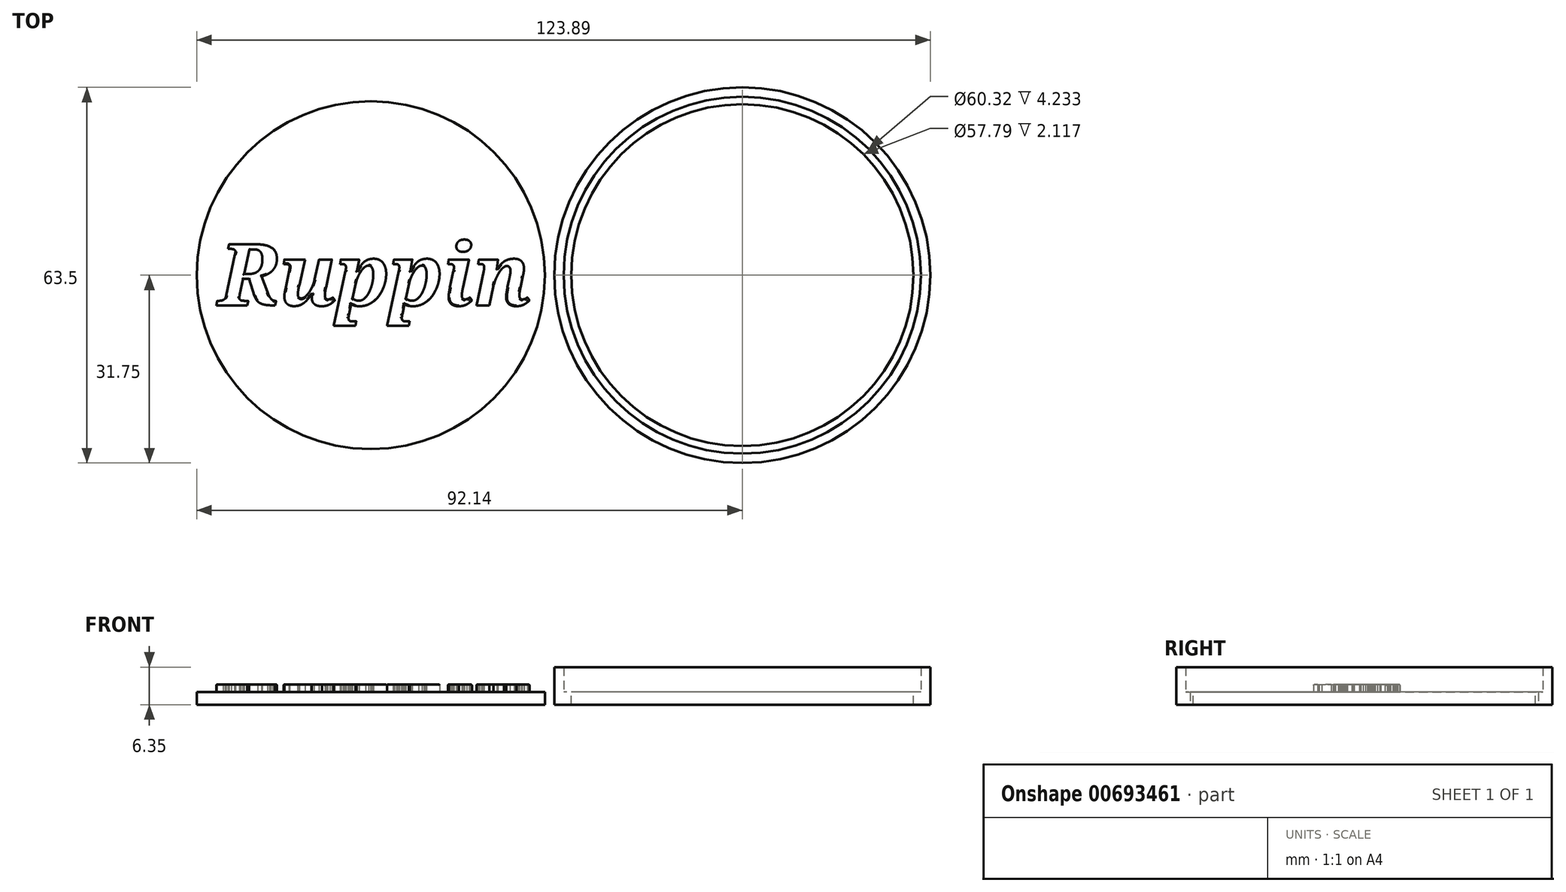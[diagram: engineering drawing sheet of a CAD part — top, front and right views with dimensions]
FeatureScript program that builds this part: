
annotation { "Feature Type Name" : "Feature", "Feature Type Description" : "" }
export const myFeature = defineFeature(function(context is Context, id is Id, definition is map)
    precondition{}
    {
        {
            var Q0;
            Q0=qCreatedBy(makeId("Top.planeOp"),FACE);
            var sketch = newSketch(context, id + "F0", { "sketchPlane" : qUnion([Q0])});
            skCircle(sketch, "E0", {"center": v(0, 0) * mm, "radius": 31.75 * mm});
            skCircle(sketch, "E1.0", {"center": v(0, 0) * mm, "radius": 30.16 * mm});
            skCircle(sketch, "E2.0", {"center": v(0, 0) * mm, "radius": 28.9 * mm});
            skCircle(sketch, "E3.0", {"center": v(0, 0) * mm, "radius": 29.4 * mm});
            skSolve(sketch);
        }
        {
            var Q0;
            Q0=makeQuery(id+"F0.imprint","IMPRINT",FACE,{"disambiguationData":[TD([[makeQuery(id+"F0.imprint","IMPRINT",EDGE,{"derivedFrom":sQuery(id+"F0.wireOp",EDGE,"E0")}),1.0]])]});
            extrude(context, id + "F1", {"entities" : qUnion([Q0]), "depth" : 2.12 * mm, "offsetDistance" : 25.4 * mm});
        }
        {
            var Q0;
            Q0=makeQuery(id+"F1.opExtrude","CAP_FACE",FACE,{"disambiguationData":[OSD([sQuery(id+"F0.wireOp",EDGE,"E0"),sQuery(id+"F0.wireOp",EDGE,"E1.0")])],"isStart":false});
            extrude(context, id + "F2", {"entities" : qUnion([Q0]), "operationType" : NewBodyOperationType.ADD, "depth" : 2.12 * mm, "offsetDistance" : 25.4 * mm});
        }
        {
            var Q0;
            Q0=makeQuery(id+"F0.imprint","IMPRINT",FACE,{"disambiguationData":[TD([[makeQuery(id+"F0.imprint","IMPRINT",EDGE,{"derivedFrom":sQuery(id+"F0.wireOp",EDGE,"E1.0")}),1.0]])]});
            var Q1;
            Q1=makeQuery(id+"F0.imprint","IMPRINT",FACE,{"disambiguationData":[TD([[makeQuery(id+"F0.imprint","IMPRINT",EDGE,{"derivedFrom":sQuery(id+"F0.wireOp",EDGE,"E0")}),1.0]])]});
            var Q2;
            Q2=makeQuery(id+"F0.imprint","IMPRINT",FACE,{"disambiguationData":[TD([[makeQuery(id+"F0.imprint","IMPRINT",EDGE,{"derivedFrom":sQuery(id+"F0.wireOp",EDGE,"E2.0")}),-1.0]])]});
            extrude(context, id + "F3", {"entities" : qUnion([Q0, Q1, Q2]), "operationType" : NewBodyOperationType.ADD, "oppositeDirection" : true, "depth" : 2.12 * mm, "offsetDistance" : 25.4 * mm});
        }
        {
            var Q0;
            Q0=makeQuery(id+"F0.imprint","IMPRINT",FACE,{"disambiguationData":[TD([[makeQuery(id+"F0.imprint","IMPRINT",EDGE,{"derivedFrom":sQuery(id+"F0.wireOp",EDGE,"E2.0")}),1.0]])]});
            var Q1;
            Q1=makeQuery(id+"F0.imprint","IMPRINT",FACE,{"disambiguationData":[TD([[makeQuery(id+"F0.imprint","IMPRINT",EDGE,{"derivedFrom":sQuery(id+"F0.wireOp",EDGE,"E2.0")}),-1.0]])]});
            extrude(context, id + "F4", {"entities" : qUnion([Q0, Q1]), "depth" : 2.12 * mm, "offsetDistance" : 25.4 * mm});
        }
        {
            var Q0;
            Q0=makeQuery(id+"F4.opExtrude","CAP_FACE",FACE,{"disambiguationData":[OSD([sQuery(id+"F0.wireOp",EDGE,"E3.0")])],"isStart":false});
            var sketch = newSketch(context, id + "F5", { "sketchPlane" : qUnion([Q0])});
            skText(sketch, "E4", { "text": "Ruppin", "fontName": "NotoSerif-BoldItalic.ttf"});
            const initialGuessF5  = {"E4": [-0.02578, -0.00511, 1, 0, 0.01041]};
            skSetInitialGuess(sketch, initialGuessF5);
            skSolve(sketch);
        }
        {
            var Q0;
            Q0=qSketchRegion(id+"F5",true);
            extrude(context, id + "F6", {"entities" : qUnion([Q0]), "operationType" : NewBodyOperationType.ADD, "depth" : 1.27 * mm, "offsetDistance" : 25.4 * mm});
        }
        {
            var Q0;
            Q0=makeQuery(id+"F6.opExtrude","CAP_FACE",FACE,{"disambiguationData":[OSD([sQuery(id+"F5.wireOp",EDGE,"E4.sketch_text.stroke-0"),sQuery(id+"F5.wireOp",EDGE,"E4.sketch_text.stroke-1"),sQuery(id+"F5.wireOp",EDGE,"E4.sketch_text.stroke-2"),sQuery(id+"F5.wireOp",EDGE,"E4.sketch_text.stroke-3"),sQuery(id+"F5.wireOp",EDGE,"E4.sketch_text.stroke-4"),sQuery(id+"F5.wireOp",EDGE,"E4.sketch_text.stroke-5"),sQuery(id+"F5.wireOp",EDGE,"E4.sketch_text.stroke-6"),sQuery(id+"F5.wireOp",EDGE,"E4.sketch_text.stroke-7"),sQuery(id+"F5.wireOp",EDGE,"E4.sketch_text.stroke-8"),sQuery(id+"F5.wireOp",EDGE,"E4.sketch_text.stroke-9"),sQuery(id+"F5.wireOp",EDGE,"E4.sketch_text.stroke-10"),sQuery(id+"F5.wireOp",EDGE,"E4.sketch_text.stroke-11"),sQuery(id+"F5.wireOp",EDGE,"E4.sketch_text.stroke-12"),sQuery(id+"F5.wireOp",EDGE,"E4.sketch_text.stroke-13"),sQuery(id+"F5.wireOp",EDGE,"E4.sketch_text.stroke-14"),sQuery(id+"F5.wireOp",EDGE,"E4.sketch_text.stroke-15"),sQuery(id+"F5.wireOp",EDGE,"E4.sketch_text.stroke-16"),sQuery(id+"F5.wireOp",EDGE,"E4.sketch_text.stroke-17"),sQuery(id+"F5.wireOp",EDGE,"E4.sketch_text.stroke-18"),sQuery(id+"F5.wireOp",EDGE,"E4.sketch_text.stroke-19"),sQuery(id+"F5.wireOp",EDGE,"E4.sketch_text.stroke-20"),sQuery(id+"F5.wireOp",EDGE,"E4.sketch_text.stroke-21"),sQuery(id+"F5.wireOp",EDGE,"E4.sketch_text.stroke-22"),sQuery(id+"F5.wireOp",EDGE,"E4.sketch_text.stroke-23"),sQuery(id+"F5.wireOp",EDGE,"E4.sketch_text.stroke-24"),sQuery(id+"F5.wireOp",EDGE,"E4.sketch_text.stroke-25"),sQuery(id+"F5.wireOp",EDGE,"E4.sketch_text.stroke-26"),sQuery(id+"F5.wireOp",EDGE,"E4.sketch_text.stroke-27"),sQuery(id+"F5.wireOp",EDGE,"E4.sketch_text.stroke-28"),sQuery(id+"F5.wireOp",EDGE,"E4.sketch_text.stroke-29"),sQuery(id+"F5.wireOp",EDGE,"E4.sketch_text.stroke-30"),sQuery(id+"F5.wireOp",EDGE,"E4.sketch_text.stroke-31"),sQuery(id+"F5.wireOp",EDGE,"E4.sketch_text.stroke-32"),sQuery(id+"F5.wireOp",EDGE,"E4.sketch_text.stroke-33"),sQuery(id+"F5.wireOp",EDGE,"E4.sketch_text.stroke-34"),sQuery(id+"F5.wireOp",EDGE,"E4.sketch_text.stroke-35"),sQuery(id+"F5.wireOp",EDGE,"E4.sketch_text.stroke-36"),sQuery(id+"F5.wireOp",EDGE,"E4.sketch_text.stroke-37"),sQuery(id+"F5.wireOp",EDGE,"E4.sketch_text.stroke-38"),sQuery(id+"F5.wireOp",EDGE,"E4.sketch_text.stroke-39"),sQuery(id+"F5.wireOp",EDGE,"E4.sketch_text.stroke-40"),sQuery(id+"F5.wireOp",EDGE,"E4.sketch_text.stroke-41"),sQuery(id+"F5.wireOp",EDGE,"E4.sketch_text.stroke-42"),sQuery(id+"F5.wireOp",EDGE,"E4.sketch_text.stroke-43"),sQuery(id+"F5.wireOp",EDGE,"E4.sketch_text.stroke-44"),sQuery(id+"F5.wireOp",EDGE,"E4.sketch_text.stroke-45"),sQuery(id+"F5.wireOp",EDGE,"E4.sketch_text.stroke-46"),sQuery(id+"F5.wireOp",EDGE,"E4.sketch_text.stroke-47"),sQuery(id+"F5.wireOp",EDGE,"E4.sketch_text.stroke-48"),sQuery(id+"F5.wireOp",EDGE,"E4.sketch_text.stroke-49"),sQuery(id+"F5.wireOp",EDGE,"E4.sketch_text.stroke-50"),sQuery(id+"F5.wireOp",EDGE,"E4.sketch_text.stroke-51"),sQuery(id+"F5.wireOp",EDGE,"E4.sketch_text.stroke-52"),sQuery(id+"F5.wireOp",EDGE,"E4.sketch_text.stroke-53"),sQuery(id+"F5.wireOp",EDGE,"E4.sketch_text.stroke-54"),sQuery(id+"F5.wireOp",EDGE,"E4.sketch_text.stroke-55")])],"isStart":false});
            var Q1;
            Q1=makeQuery(id+"F6.opExtrude","CAP_FACE",FACE,{"disambiguationData":[OSD([sQuery(id+"F5.wireOp",EDGE,"E4.sketch_text.stroke-56"),sQuery(id+"F5.wireOp",EDGE,"E4.sketch_text.stroke-57"),sQuery(id+"F5.wireOp",EDGE,"E4.sketch_text.stroke-58"),sQuery(id+"F5.wireOp",EDGE,"E4.sketch_text.stroke-59"),sQuery(id+"F5.wireOp",EDGE,"E4.sketch_text.stroke-60"),sQuery(id+"F5.wireOp",EDGE,"E4.sketch_text.stroke-61"),sQuery(id+"F5.wireOp",EDGE,"E4.sketch_text.stroke-62"),sQuery(id+"F5.wireOp",EDGE,"E4.sketch_text.stroke-63"),sQuery(id+"F5.wireOp",EDGE,"E4.sketch_text.stroke-64"),sQuery(id+"F5.wireOp",EDGE,"E4.sketch_text.stroke-65"),sQuery(id+"F5.wireOp",EDGE,"E4.sketch_text.stroke-66"),sQuery(id+"F5.wireOp",EDGE,"E4.sketch_text.stroke-67"),sQuery(id+"F5.wireOp",EDGE,"E4.sketch_text.stroke-68"),sQuery(id+"F5.wireOp",EDGE,"E4.sketch_text.stroke-69"),sQuery(id+"F5.wireOp",EDGE,"E4.sketch_text.stroke-70"),sQuery(id+"F5.wireOp",EDGE,"E4.sketch_text.stroke-71"),sQuery(id+"F5.wireOp",EDGE,"E4.sketch_text.stroke-72"),sQuery(id+"F5.wireOp",EDGE,"E4.sketch_text.stroke-73"),sQuery(id+"F5.wireOp",EDGE,"E4.sketch_text.stroke-74"),sQuery(id+"F5.wireOp",EDGE,"E4.sketch_text.stroke-75"),sQuery(id+"F5.wireOp",EDGE,"E4.sketch_text.stroke-76"),sQuery(id+"F5.wireOp",EDGE,"E4.sketch_text.stroke-77"),sQuery(id+"F5.wireOp",EDGE,"E4.sketch_text.stroke-78"),sQuery(id+"F5.wireOp",EDGE,"E4.sketch_text.stroke-79"),sQuery(id+"F5.wireOp",EDGE,"E4.sketch_text.stroke-80"),sQuery(id+"F5.wireOp",EDGE,"E4.sketch_text.stroke-81"),sQuery(id+"F5.wireOp",EDGE,"E4.sketch_text.stroke-82"),sQuery(id+"F5.wireOp",EDGE,"E4.sketch_text.stroke-83"),sQuery(id+"F5.wireOp",EDGE,"E4.sketch_text.stroke-84"),sQuery(id+"F5.wireOp",EDGE,"E4.sketch_text.stroke-85"),sQuery(id+"F5.wireOp",EDGE,"E4.sketch_text.stroke-86"),sQuery(id+"F5.wireOp",EDGE,"E4.sketch_text.stroke-87"),sQuery(id+"F5.wireOp",EDGE,"E4.sketch_text.stroke-88"),sQuery(id+"F5.wireOp",EDGE,"E4.sketch_text.stroke-89"),sQuery(id+"F5.wireOp",EDGE,"E4.sketch_text.stroke-90"),sQuery(id+"F5.wireOp",EDGE,"E4.sketch_text.stroke-91"),sQuery(id+"F5.wireOp",EDGE,"E4.sketch_text.stroke-92"),sQuery(id+"F5.wireOp",EDGE,"E4.sketch_text.stroke-93"),sQuery(id+"F5.wireOp",EDGE,"E4.sketch_text.stroke-94"),sQuery(id+"F5.wireOp",EDGE,"E4.sketch_text.stroke-95"),sQuery(id+"F5.wireOp",EDGE,"E4.sketch_text.stroke-96"),sQuery(id+"F5.wireOp",EDGE,"E4.sketch_text.stroke-97"),sQuery(id+"F5.wireOp",EDGE,"E4.sketch_text.stroke-98"),sQuery(id+"F5.wireOp",EDGE,"E4.sketch_text.stroke-99"),sQuery(id+"F5.wireOp",EDGE,"E4.sketch_text.stroke-100"),sQuery(id+"F5.wireOp",EDGE,"E4.sketch_text.stroke-101"),sQuery(id+"F5.wireOp",EDGE,"E4.sketch_text.stroke-102"),sQuery(id+"F5.wireOp",EDGE,"E4.sketch_text.stroke-103"),sQuery(id+"F5.wireOp",EDGE,"E4.sketch_text.stroke-104"),sQuery(id+"F5.wireOp",EDGE,"E4.sketch_text.stroke-105"),sQuery(id+"F5.wireOp",EDGE,"E4.sketch_text.stroke-106"),sQuery(id+"F5.wireOp",EDGE,"E4.sketch_text.stroke-107")])],"isStart":false});
            var Q2;
            Q2=makeQuery(id+"F6.opExtrude","CAP_FACE",FACE,{"disambiguationData":[OSD([sQuery(id+"F5.wireOp",EDGE,"E4.sketch_text.stroke-108"),sQuery(id+"F5.wireOp",EDGE,"E4.sketch_text.stroke-109"),sQuery(id+"F5.wireOp",EDGE,"E4.sketch_text.stroke-110"),sQuery(id+"F5.wireOp",EDGE,"E4.sketch_text.stroke-111"),sQuery(id+"F5.wireOp",EDGE,"E4.sketch_text.stroke-112"),sQuery(id+"F5.wireOp",EDGE,"E4.sketch_text.stroke-113"),sQuery(id+"F5.wireOp",EDGE,"E4.sketch_text.stroke-114"),sQuery(id+"F5.wireOp",EDGE,"E4.sketch_text.stroke-115"),sQuery(id+"F5.wireOp",EDGE,"E4.sketch_text.stroke-116"),sQuery(id+"F5.wireOp",EDGE,"E4.sketch_text.stroke-117"),sQuery(id+"F5.wireOp",EDGE,"E4.sketch_text.stroke-118"),sQuery(id+"F5.wireOp",EDGE,"E4.sketch_text.stroke-119"),sQuery(id+"F5.wireOp",EDGE,"E4.sketch_text.stroke-120"),sQuery(id+"F5.wireOp",EDGE,"E4.sketch_text.stroke-121"),sQuery(id+"F5.wireOp",EDGE,"E4.sketch_text.stroke-122"),sQuery(id+"F5.wireOp",EDGE,"E4.sketch_text.stroke-123"),sQuery(id+"F5.wireOp",EDGE,"E4.sketch_text.stroke-124"),sQuery(id+"F5.wireOp",EDGE,"E4.sketch_text.stroke-125"),sQuery(id+"F5.wireOp",EDGE,"E4.sketch_text.stroke-126"),sQuery(id+"F5.wireOp",EDGE,"E4.sketch_text.stroke-127"),sQuery(id+"F5.wireOp",EDGE,"E4.sketch_text.stroke-128"),sQuery(id+"F5.wireOp",EDGE,"E4.sketch_text.stroke-129"),sQuery(id+"F5.wireOp",EDGE,"E4.sketch_text.stroke-130"),sQuery(id+"F5.wireOp",EDGE,"E4.sketch_text.stroke-131"),sQuery(id+"F5.wireOp",EDGE,"E4.sketch_text.stroke-132"),sQuery(id+"F5.wireOp",EDGE,"E4.sketch_text.stroke-133"),sQuery(id+"F5.wireOp",EDGE,"E4.sketch_text.stroke-134"),sQuery(id+"F5.wireOp",EDGE,"E4.sketch_text.stroke-135"),sQuery(id+"F5.wireOp",EDGE,"E4.sketch_text.stroke-136"),sQuery(id+"F5.wireOp",EDGE,"E4.sketch_text.stroke-137"),sQuery(id+"F5.wireOp",EDGE,"E4.sketch_text.stroke-138"),sQuery(id+"F5.wireOp",EDGE,"E4.sketch_text.stroke-139"),sQuery(id+"F5.wireOp",EDGE,"E4.sketch_text.stroke-140"),sQuery(id+"F5.wireOp",EDGE,"E4.sketch_text.stroke-141"),sQuery(id+"F5.wireOp",EDGE,"E4.sketch_text.stroke-142"),sQuery(id+"F5.wireOp",EDGE,"E4.sketch_text.stroke-143"),sQuery(id+"F5.wireOp",EDGE,"E4.sketch_text.stroke-144"),sQuery(id+"F5.wireOp",EDGE,"E4.sketch_text.stroke-145"),sQuery(id+"F5.wireOp",EDGE,"E4.sketch_text.stroke-146"),sQuery(id+"F5.wireOp",EDGE,"E4.sketch_text.stroke-147"),sQuery(id+"F5.wireOp",EDGE,"E4.sketch_text.stroke-148"),sQuery(id+"F5.wireOp",EDGE,"E4.sketch_text.stroke-149"),sQuery(id+"F5.wireOp",EDGE,"E4.sketch_text.stroke-150"),sQuery(id+"F5.wireOp",EDGE,"E4.sketch_text.stroke-151"),sQuery(id+"F5.wireOp",EDGE,"E4.sketch_text.stroke-152"),sQuery(id+"F5.wireOp",EDGE,"E4.sketch_text.stroke-153"),sQuery(id+"F5.wireOp",EDGE,"E4.sketch_text.stroke-154"),sQuery(id+"F5.wireOp",EDGE,"E4.sketch_text.stroke-155"),sQuery(id+"F5.wireOp",EDGE,"E4.sketch_text.stroke-156"),sQuery(id+"F5.wireOp",EDGE,"E4.sketch_text.stroke-157"),sQuery(id+"F5.wireOp",EDGE,"E4.sketch_text.stroke-158"),sQuery(id+"F5.wireOp",EDGE,"E4.sketch_text.stroke-159"),sQuery(id+"F5.wireOp",EDGE,"E4.sketch_text.stroke-160"),sQuery(id+"F5.wireOp",EDGE,"E4.sketch_text.stroke-161"),sQuery(id+"F5.wireOp",EDGE,"E4.sketch_text.stroke-162"),sQuery(id+"F5.wireOp",EDGE,"E4.sketch_text.stroke-163"),sQuery(id+"F5.wireOp",EDGE,"E4.sketch_text.stroke-164"),sQuery(id+"F5.wireOp",EDGE,"E4.sketch_text.stroke-165"),sQuery(id+"F5.wireOp",EDGE,"E4.sketch_text.stroke-166"),sQuery(id+"F5.wireOp",EDGE,"E4.sketch_text.stroke-167"),sQuery(id+"F5.wireOp",EDGE,"E4.sketch_text.stroke-168"),sQuery(id+"F5.wireOp",EDGE,"E4.sketch_text.stroke-169"),sQuery(id+"F5.wireOp",EDGE,"E4.sketch_text.stroke-170"),sQuery(id+"F5.wireOp",EDGE,"E4.sketch_text.stroke-171"),sQuery(id+"F5.wireOp",EDGE,"E4.sketch_text.stroke-172"),sQuery(id+"F5.wireOp",EDGE,"E4.sketch_text.stroke-173")])],"isStart":false});
            var Q3;
            Q3=makeQuery(id+"F6.opExtrude","CAP_FACE",FACE,{"disambiguationData":[OSD([sQuery(id+"F5.wireOp",EDGE,"E4.sketch_text.stroke-174"),sQuery(id+"F5.wireOp",EDGE,"E4.sketch_text.stroke-175"),sQuery(id+"F5.wireOp",EDGE,"E4.sketch_text.stroke-176"),sQuery(id+"F5.wireOp",EDGE,"E4.sketch_text.stroke-177"),sQuery(id+"F5.wireOp",EDGE,"E4.sketch_text.stroke-178"),sQuery(id+"F5.wireOp",EDGE,"E4.sketch_text.stroke-179"),sQuery(id+"F5.wireOp",EDGE,"E4.sketch_text.stroke-180"),sQuery(id+"F5.wireOp",EDGE,"E4.sketch_text.stroke-181"),sQuery(id+"F5.wireOp",EDGE,"E4.sketch_text.stroke-182"),sQuery(id+"F5.wireOp",EDGE,"E4.sketch_text.stroke-183"),sQuery(id+"F5.wireOp",EDGE,"E4.sketch_text.stroke-184"),sQuery(id+"F5.wireOp",EDGE,"E4.sketch_text.stroke-185"),sQuery(id+"F5.wireOp",EDGE,"E4.sketch_text.stroke-186"),sQuery(id+"F5.wireOp",EDGE,"E4.sketch_text.stroke-187"),sQuery(id+"F5.wireOp",EDGE,"E4.sketch_text.stroke-188"),sQuery(id+"F5.wireOp",EDGE,"E4.sketch_text.stroke-189"),sQuery(id+"F5.wireOp",EDGE,"E4.sketch_text.stroke-190"),sQuery(id+"F5.wireOp",EDGE,"E4.sketch_text.stroke-191"),sQuery(id+"F5.wireOp",EDGE,"E4.sketch_text.stroke-192"),sQuery(id+"F5.wireOp",EDGE,"E4.sketch_text.stroke-193"),sQuery(id+"F5.wireOp",EDGE,"E4.sketch_text.stroke-194"),sQuery(id+"F5.wireOp",EDGE,"E4.sketch_text.stroke-195"),sQuery(id+"F5.wireOp",EDGE,"E4.sketch_text.stroke-196"),sQuery(id+"F5.wireOp",EDGE,"E4.sketch_text.stroke-197"),sQuery(id+"F5.wireOp",EDGE,"E4.sketch_text.stroke-198"),sQuery(id+"F5.wireOp",EDGE,"E4.sketch_text.stroke-199"),sQuery(id+"F5.wireOp",EDGE,"E4.sketch_text.stroke-200"),sQuery(id+"F5.wireOp",EDGE,"E4.sketch_text.stroke-201"),sQuery(id+"F5.wireOp",EDGE,"E4.sketch_text.stroke-202"),sQuery(id+"F5.wireOp",EDGE,"E4.sketch_text.stroke-203"),sQuery(id+"F5.wireOp",EDGE,"E4.sketch_text.stroke-204"),sQuery(id+"F5.wireOp",EDGE,"E4.sketch_text.stroke-205"),sQuery(id+"F5.wireOp",EDGE,"E4.sketch_text.stroke-206"),sQuery(id+"F5.wireOp",EDGE,"E4.sketch_text.stroke-207"),sQuery(id+"F5.wireOp",EDGE,"E4.sketch_text.stroke-208"),sQuery(id+"F5.wireOp",EDGE,"E4.sketch_text.stroke-209"),sQuery(id+"F5.wireOp",EDGE,"E4.sketch_text.stroke-210"),sQuery(id+"F5.wireOp",EDGE,"E4.sketch_text.stroke-211"),sQuery(id+"F5.wireOp",EDGE,"E4.sketch_text.stroke-212"),sQuery(id+"F5.wireOp",EDGE,"E4.sketch_text.stroke-213"),sQuery(id+"F5.wireOp",EDGE,"E4.sketch_text.stroke-214"),sQuery(id+"F5.wireOp",EDGE,"E4.sketch_text.stroke-215"),sQuery(id+"F5.wireOp",EDGE,"E4.sketch_text.stroke-216"),sQuery(id+"F5.wireOp",EDGE,"E4.sketch_text.stroke-217"),sQuery(id+"F5.wireOp",EDGE,"E4.sketch_text.stroke-218"),sQuery(id+"F5.wireOp",EDGE,"E4.sketch_text.stroke-219"),sQuery(id+"F5.wireOp",EDGE,"E4.sketch_text.stroke-220"),sQuery(id+"F5.wireOp",EDGE,"E4.sketch_text.stroke-221"),sQuery(id+"F5.wireOp",EDGE,"E4.sketch_text.stroke-222"),sQuery(id+"F5.wireOp",EDGE,"E4.sketch_text.stroke-223"),sQuery(id+"F5.wireOp",EDGE,"E4.sketch_text.stroke-224"),sQuery(id+"F5.wireOp",EDGE,"E4.sketch_text.stroke-225"),sQuery(id+"F5.wireOp",EDGE,"E4.sketch_text.stroke-226"),sQuery(id+"F5.wireOp",EDGE,"E4.sketch_text.stroke-227"),sQuery(id+"F5.wireOp",EDGE,"E4.sketch_text.stroke-228"),sQuery(id+"F5.wireOp",EDGE,"E4.sketch_text.stroke-229"),sQuery(id+"F5.wireOp",EDGE,"E4.sketch_text.stroke-230"),sQuery(id+"F5.wireOp",EDGE,"E4.sketch_text.stroke-231"),sQuery(id+"F5.wireOp",EDGE,"E4.sketch_text.stroke-232"),sQuery(id+"F5.wireOp",EDGE,"E4.sketch_text.stroke-233"),sQuery(id+"F5.wireOp",EDGE,"E4.sketch_text.stroke-234"),sQuery(id+"F5.wireOp",EDGE,"E4.sketch_text.stroke-235"),sQuery(id+"F5.wireOp",EDGE,"E4.sketch_text.stroke-236"),sQuery(id+"F5.wireOp",EDGE,"E4.sketch_text.stroke-237"),sQuery(id+"F5.wireOp",EDGE,"E4.sketch_text.stroke-238"),sQuery(id+"F5.wireOp",EDGE,"E4.sketch_text.stroke-239")])],"isStart":false});
            var Q4;
            Q4=makeQuery(id+"F6.opExtrude","CAP_FACE",FACE,{"disambiguationData":[OSD([sQuery(id+"F5.wireOp",EDGE,"E4.sketch_text.stroke-240"),sQuery(id+"F5.wireOp",EDGE,"E4.sketch_text.stroke-241"),sQuery(id+"F5.wireOp",EDGE,"E4.sketch_text.stroke-242"),sQuery(id+"F5.wireOp",EDGE,"E4.sketch_text.stroke-243"),sQuery(id+"F5.wireOp",EDGE,"E4.sketch_text.stroke-244"),sQuery(id+"F5.wireOp",EDGE,"E4.sketch_text.stroke-245"),sQuery(id+"F5.wireOp",EDGE,"E4.sketch_text.stroke-246"),sQuery(id+"F5.wireOp",EDGE,"E4.sketch_text.stroke-247"),sQuery(id+"F5.wireOp",EDGE,"E4.sketch_text.stroke-248"),sQuery(id+"F5.wireOp",EDGE,"E4.sketch_text.stroke-249"),sQuery(id+"F5.wireOp",EDGE,"E4.sketch_text.stroke-250"),sQuery(id+"F5.wireOp",EDGE,"E4.sketch_text.stroke-251"),sQuery(id+"F5.wireOp",EDGE,"E4.sketch_text.stroke-252"),sQuery(id+"F5.wireOp",EDGE,"E4.sketch_text.stroke-253"),sQuery(id+"F5.wireOp",EDGE,"E4.sketch_text.stroke-254"),sQuery(id+"F5.wireOp",EDGE,"E4.sketch_text.stroke-255"),sQuery(id+"F5.wireOp",EDGE,"E4.sketch_text.stroke-256"),sQuery(id+"F5.wireOp",EDGE,"E4.sketch_text.stroke-257"),sQuery(id+"F5.wireOp",EDGE,"E4.sketch_text.stroke-258"),sQuery(id+"F5.wireOp",EDGE,"E4.sketch_text.stroke-259"),sQuery(id+"F5.wireOp",EDGE,"E4.sketch_text.stroke-260"),sQuery(id+"F5.wireOp",EDGE,"E4.sketch_text.stroke-261"),sQuery(id+"F5.wireOp",EDGE,"E4.sketch_text.stroke-262"),sQuery(id+"F5.wireOp",EDGE,"E4.sketch_text.stroke-263"),sQuery(id+"F5.wireOp",EDGE,"E4.sketch_text.stroke-264"),sQuery(id+"F5.wireOp",EDGE,"E4.sketch_text.stroke-265"),sQuery(id+"F5.wireOp",EDGE,"E4.sketch_text.stroke-266"),sQuery(id+"F5.wireOp",EDGE,"E4.sketch_text.stroke-267")])],"isStart":false});
            var Q5;
            Q5=makeQuery(id+"F6.opExtrude","CAP_FACE",FACE,{"disambiguationData":[OSD([sQuery(id+"F5.wireOp",EDGE,"E4.sketch_text.stroke-284"),sQuery(id+"F5.wireOp",EDGE,"E4.sketch_text.stroke-285"),sQuery(id+"F5.wireOp",EDGE,"E4.sketch_text.stroke-286"),sQuery(id+"F5.wireOp",EDGE,"E4.sketch_text.stroke-287"),sQuery(id+"F5.wireOp",EDGE,"E4.sketch_text.stroke-288"),sQuery(id+"F5.wireOp",EDGE,"E4.sketch_text.stroke-289"),sQuery(id+"F5.wireOp",EDGE,"E4.sketch_text.stroke-290"),sQuery(id+"F5.wireOp",EDGE,"E4.sketch_text.stroke-291"),sQuery(id+"F5.wireOp",EDGE,"E4.sketch_text.stroke-292"),sQuery(id+"F5.wireOp",EDGE,"E4.sketch_text.stroke-293"),sQuery(id+"F5.wireOp",EDGE,"E4.sketch_text.stroke-294"),sQuery(id+"F5.wireOp",EDGE,"E4.sketch_text.stroke-295"),sQuery(id+"F5.wireOp",EDGE,"E4.sketch_text.stroke-296"),sQuery(id+"F5.wireOp",EDGE,"E4.sketch_text.stroke-297"),sQuery(id+"F5.wireOp",EDGE,"E4.sketch_text.stroke-298"),sQuery(id+"F5.wireOp",EDGE,"E4.sketch_text.stroke-299"),sQuery(id+"F5.wireOp",EDGE,"E4.sketch_text.stroke-300"),sQuery(id+"F5.wireOp",EDGE,"E4.sketch_text.stroke-301"),sQuery(id+"F5.wireOp",EDGE,"E4.sketch_text.stroke-302"),sQuery(id+"F5.wireOp",EDGE,"E4.sketch_text.stroke-303"),sQuery(id+"F5.wireOp",EDGE,"E4.sketch_text.stroke-304"),sQuery(id+"F5.wireOp",EDGE,"E4.sketch_text.stroke-305"),sQuery(id+"F5.wireOp",EDGE,"E4.sketch_text.stroke-306"),sQuery(id+"F5.wireOp",EDGE,"E4.sketch_text.stroke-307"),sQuery(id+"F5.wireOp",EDGE,"E4.sketch_text.stroke-308"),sQuery(id+"F5.wireOp",EDGE,"E4.sketch_text.stroke-309"),sQuery(id+"F5.wireOp",EDGE,"E4.sketch_text.stroke-310"),sQuery(id+"F5.wireOp",EDGE,"E4.sketch_text.stroke-311"),sQuery(id+"F5.wireOp",EDGE,"E4.sketch_text.stroke-312"),sQuery(id+"F5.wireOp",EDGE,"E4.sketch_text.stroke-313"),sQuery(id+"F5.wireOp",EDGE,"E4.sketch_text.stroke-314"),sQuery(id+"F5.wireOp",EDGE,"E4.sketch_text.stroke-315"),sQuery(id+"F5.wireOp",EDGE,"E4.sketch_text.stroke-316"),sQuery(id+"F5.wireOp",EDGE,"E4.sketch_text.stroke-317"),sQuery(id+"F5.wireOp",EDGE,"E4.sketch_text.stroke-318"),sQuery(id+"F5.wireOp",EDGE,"E4.sketch_text.stroke-319"),sQuery(id+"F5.wireOp",EDGE,"E4.sketch_text.stroke-320"),sQuery(id+"F5.wireOp",EDGE,"E4.sketch_text.stroke-321"),sQuery(id+"F5.wireOp",EDGE,"E4.sketch_text.stroke-322"),sQuery(id+"F5.wireOp",EDGE,"E4.sketch_text.stroke-323"),sQuery(id+"F5.wireOp",EDGE,"E4.sketch_text.stroke-324"),sQuery(id+"F5.wireOp",EDGE,"E4.sketch_text.stroke-325"),sQuery(id+"F5.wireOp",EDGE,"E4.sketch_text.stroke-326"),sQuery(id+"F5.wireOp",EDGE,"E4.sketch_text.stroke-327"),sQuery(id+"F5.wireOp",EDGE,"E4.sketch_text.stroke-328"),sQuery(id+"F5.wireOp",EDGE,"E4.sketch_text.stroke-329"),sQuery(id+"F5.wireOp",EDGE,"E4.sketch_text.stroke-330"),sQuery(id+"F5.wireOp",EDGE,"E4.sketch_text.stroke-331"),sQuery(id+"F5.wireOp",EDGE,"E4.sketch_text.stroke-332"),sQuery(id+"F5.wireOp",EDGE,"E4.sketch_text.stroke-333"),sQuery(id+"F5.wireOp",EDGE,"E4.sketch_text.stroke-334"),sQuery(id+"F5.wireOp",EDGE,"E4.sketch_text.stroke-335"),sQuery(id+"F5.wireOp",EDGE,"E4.sketch_text.stroke-336"),sQuery(id+"F5.wireOp",EDGE,"E4.sketch_text.stroke-337"),sQuery(id+"F5.wireOp",EDGE,"E4.sketch_text.stroke-338"),sQuery(id+"F5.wireOp",EDGE,"E4.sketch_text.stroke-339"),sQuery(id+"F5.wireOp",EDGE,"E4.sketch_text.stroke-340"),sQuery(id+"F5.wireOp",EDGE,"E4.sketch_text.stroke-341")])],"isStart":false});
            var Q6;
            Q6=makeQuery(id+"F6.opExtrude","CAP_FACE",FACE,{"disambiguationData":[OSD([sQuery(id+"F5.wireOp",EDGE,"E4.sketch_text.stroke-268"),sQuery(id+"F5.wireOp",EDGE,"E4.sketch_text.stroke-269"),sQuery(id+"F5.wireOp",EDGE,"E4.sketch_text.stroke-270"),sQuery(id+"F5.wireOp",EDGE,"E4.sketch_text.stroke-271"),sQuery(id+"F5.wireOp",EDGE,"E4.sketch_text.stroke-272"),sQuery(id+"F5.wireOp",EDGE,"E4.sketch_text.stroke-273"),sQuery(id+"F5.wireOp",EDGE,"E4.sketch_text.stroke-274"),sQuery(id+"F5.wireOp",EDGE,"E4.sketch_text.stroke-275"),sQuery(id+"F5.wireOp",EDGE,"E4.sketch_text.stroke-276"),sQuery(id+"F5.wireOp",EDGE,"E4.sketch_text.stroke-277"),sQuery(id+"F5.wireOp",EDGE,"E4.sketch_text.stroke-278"),sQuery(id+"F5.wireOp",EDGE,"E4.sketch_text.stroke-279"),sQuery(id+"F5.wireOp",EDGE,"E4.sketch_text.stroke-280"),sQuery(id+"F5.wireOp",EDGE,"E4.sketch_text.stroke-281"),sQuery(id+"F5.wireOp",EDGE,"E4.sketch_text.stroke-282"),sQuery(id+"F5.wireOp",EDGE,"E4.sketch_text.stroke-283")])],"isStart":false});
            fillet(context, id + "F7", {"entities" : qUnion([Q0, Q1, Q2, Q3, Q4, Q5, Q6]), "radius" : 0.13 * mm, "tangentPropagation" : true, "allowEdgeOverflow" : false});
        }
        {
            var Q0;
            Q0=makeQuery(id+"F4.opExtrude","SWEPT_BODY",BODY,{"disambiguationData":[OSD([sQuery(id+"F0.wireOp",EDGE,"E3.0")])]});
            transform(context, id + "F8", {"entities" : qUnion([Q0]), "transformType" : TransformType.TRANSLATION_3D, "dx" : -62.74 * mm, "dy" : 0 * mm, "dz" : 0 * mm, "makeCopy" : false});
        }
        {
            var Q0;
            Q0=makeQuery(id+"F1.opExtrude","SWEPT_BODY",BODY,{"disambiguationData":[OSD([sQuery(id+"F0.wireOp",EDGE,"E0"),sQuery(id+"F0.wireOp",EDGE,"E1.0")])]});
            transform(context, id + "F9", {"entities" : qUnion([Q0]), "transformType" : TransformType.TRANSLATION_3D, "dx" : 0 * mm, "dy" : 0 * mm, "dz" : 2.12 * mm, "makeCopy" : false});
        }
    });
